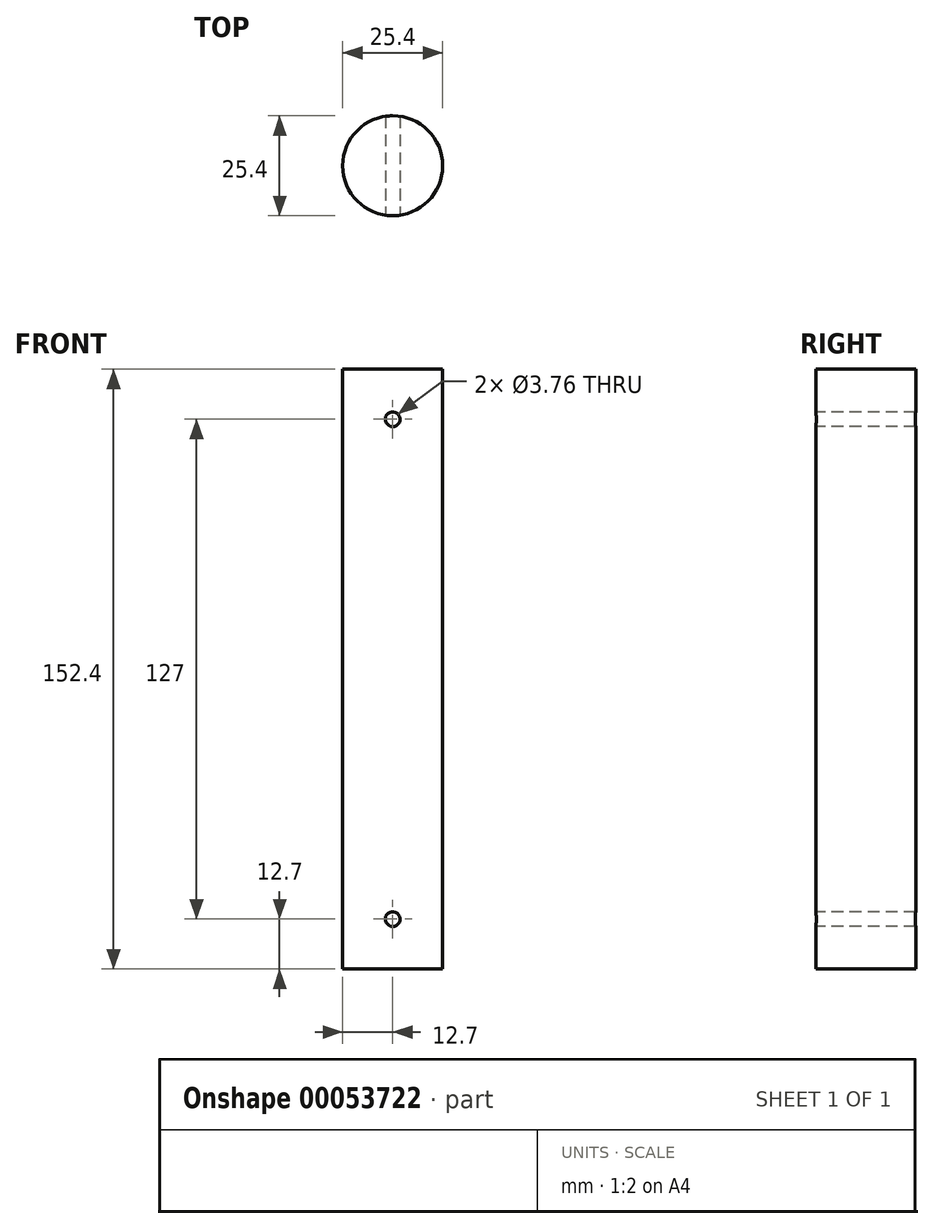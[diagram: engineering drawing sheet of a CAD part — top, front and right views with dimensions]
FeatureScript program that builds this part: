
annotation { "Feature Type Name" : "Feature", "Feature Type Description" : "" }
export const myFeature = defineFeature(function(context is Context, id is Id, definition is map)
    precondition{}
    {
        {
            var Q0;
            Q0=qCreatedBy(makeId("Top.planeOp"),FACE);
            var sketch = newSketch(context, id + "F0", { "sketchPlane" : qUnion([Q0])});
            skCircle(sketch, "E0", {"center": v(0, 0) * mm, "radius": 12.7 * mm});
            skSolve(sketch);
        }
        {
            var Q0;
            Q0 = qSketchRegion(id + "F0", true);
            extrude(context, id + "F1", {"entities" : qUnion([Q0]), "depth" : 152.4 * mm});
        }
        {
            var Q0;
            Q0=qCreatedBy(makeId("Front.planeOp"),FACE);
            var sketch = newSketch(context, id + "F2", { "sketchPlane" : qUnion([Q0])});
            skCircle(sketch, "E1", {"center": v(0, 12.7) * mm, "radius": 1.88 * mm});
            skSolve(sketch);
        }
        {
            var Q0;
            Q0 = qSketchRegion(id + "F2", true);
            extrude(context, id + "F3", {"entities" : qUnion([Q0]), "operationType" : NewBodyOperationType.REMOVE, "endBound" : BoundingType.SYMMETRIC, "oppositeDirection" : true, "depth" : 50.8 * mm});
        }
        {
            var Q0;
            Q0=qCreatedBy(makeId("Front.planeOp"),FACE);
            var sketch = newSketch(context, id + "F4", { "sketchPlane" : qUnion([Q0])});
            skLineSegment(sketch, "E2", {"start": v(0, 312.07) * mm, "end": v(0, 299.37) * mm});
            skCircle(sketch, "E3", {"center": v(0, 139.7) * mm, "radius": 1.88 * mm});
            skSolve(sketch);
        }
        {
            var Q0;
            Q0 = qSketchRegion(id + "F4", true);
            extrude(context, id + "F5", {"entities" : qUnion([Q0]), "operationType" : NewBodyOperationType.REMOVE, "endBound" : BoundingType.SYMMETRIC, "oppositeDirection" : true, "depth" : 50.8 * mm});
        }
    });
